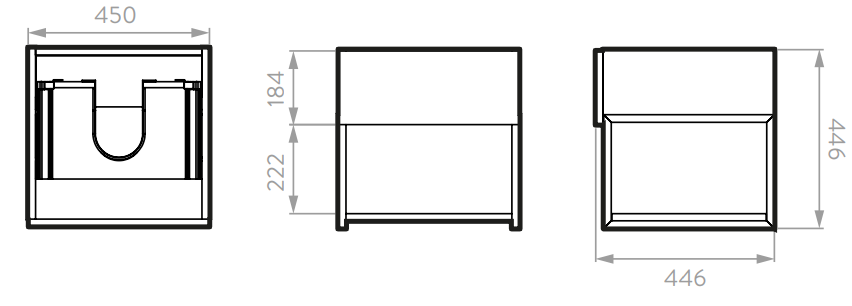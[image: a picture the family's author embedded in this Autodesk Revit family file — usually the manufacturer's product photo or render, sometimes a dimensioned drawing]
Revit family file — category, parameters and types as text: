
# Revit family: O34126491_Mueble Fussion Plus 45 cm con Lavamanos
name_source: partatom
category: Furniture
units: mm (PartAtom-declared; Revit-internal decimal feet)

## family parameters
Always vertical = Yes
Cut with Voids When Loaded = No
Host = Wall
OmniClass Number = 23.31.25.13
OmniClass Title = Bathroom Cabinets
Room Calculation Point = No
Shared = No

## types (1)
- Type 1
    Alto = 1200 mm
    Ancho = 450 mm  [stored 1.47638 ft]
    Canto = PVC rígido 22 mm de calibre.
    Creado por = BIMBAU
    Default Elevation = 0 mm  [stored 0 ft]
    Densidad = 18mm 659 kg./m^3. - 15mm 670 kg./m^3
    Description = Línea de Muebles Fussion Plus con repisa inferior expuesta e incrustaciones en aluminio que dan un toque moderno a tu baño!
    Fecha de creación = 16/03/2021
    Manufacturer = Corona
    Material = Corona_Madera_Taupe
    Material 2 = Corona_Acero_Negro Mate
    Model = Mueble Fussion Plus 45 cm con Lavamanos
    Peso Bruto aprox = 29.5 lb (13.4Kg)
    Peso Neto aprox = 24.3 lb (11Kg)
    Profundidad = 446 mm  [stored 1.46325 ft]
    Resistencia a la humedad = 8%
    Resistencia al rayado = 700 ciclos
    Textura = Taupé.
    URL = https://corona.co

note: [stored X ft] marks values corroborated as IEEE doubles in the binary element streams (Revit-internal decimal feet)

## geometry (parser evidence)
native form markers: Sweep x7
no freeform markers — native parametric forms only
